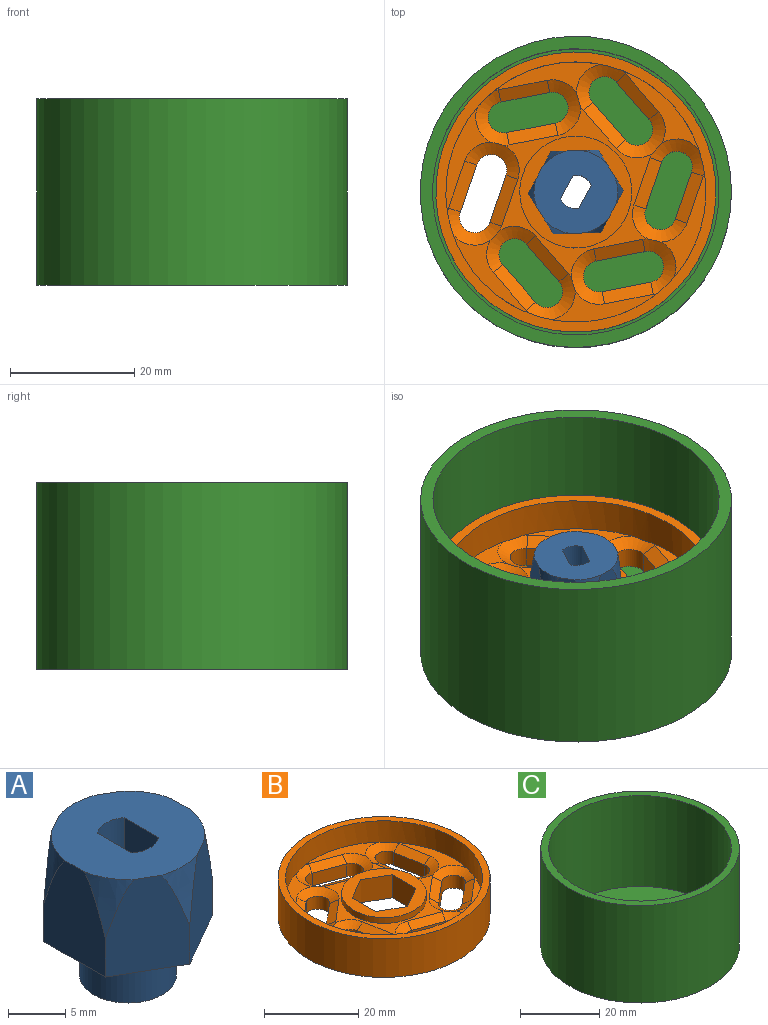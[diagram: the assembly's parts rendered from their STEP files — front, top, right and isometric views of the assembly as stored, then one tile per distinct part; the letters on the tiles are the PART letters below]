
ASSEMBLY  parts=3 mates=1
PART A: 21 faces, bbox 15.1x15.3x15 mm
  f0: plane 13.47x13.25mm, normal (0,0,1), area 124.8mm2, adj f1,f2,f3,f4,f5,f6,f7,f12
  f1: plane 10x6.63mm, normal (0.5,0.87,0), area 63.4mm2, adj f0,f2,f3,f14,f19,f20
  f2: plane 10x6.63mm, normal (-0.5,0.87,0), area 63.4mm2, adj f0,f1,f4,f14,f18,f20
  f3: plane 10x7.65mm, normal (1,0,0), area 63.4mm2, adj f0,f1,f5,f14,f17,f19
  f4: plane 10x7.65mm, normal (-1,0,0), area 63.4mm2, adj f0,f2,f6,f14,f15,f18
  f5: plane 10x6.63mm, normal (0.5,-0.87,0), area 63.4mm2, adj f0,f3,f6,f14,f16,f17
  f6: plane 10x6.63mm, normal (-0.5,-0.87,0), area 63.4mm2, adj f0,f4,f5,f14,f15,f16
  f7: cylinder r=2.7mm len=15mm, axis (0,0,-1), area 136.1mm2, adj f0,f9,f10,f11,f12,f13
  f8: cylinder r=4.25mm len=8.5mm, axis (0,0,-1), area 133.5mm2, adj f9,f14
  f9: plane 8.5x8.5mm, normal (0,0,-1), area 33.8mm2, adj f7,f8
  f10: plane 4.27x1.05mm, normal (0,0,-1), area 3.1mm2, adj f7,f13
  f11: plane 4.27x1.05mm, normal (0,0,-1), area 3.1mm2, adj f7,f12
  f12: plane 12x4.27mm, normal (-1,0,0), area 51.3mm2, adj f0,f7,f11
  f13: plane 12x4.27mm, normal (1,0,0), area 51.3mm2, adj f0,f7,f10
  f14: plane 15.3x13.25mm, normal (0,0,-1), area 95.3mm2, adj f1,f2,f3,f4,f5,f6,f8
  f15: cone r=6.59mm half-angle=8.8deg, axis (0,0,-1), area 11.5mm2, adj f0,f4,f6
  f16: cone r=6.59mm half-angle=8.8deg, axis (0,0,-1), area 11.5mm2, adj f0,f5,f6
  f17: cone r=6.59mm half-angle=8.8deg, axis (0,0,-1), area 11.5mm2, adj f0,f3,f5
  f18: cone r=6.59mm half-angle=8.8deg, axis (0,0,-1), area 11.5mm2, adj f0,f2,f4
  f19: cone r=6.59mm half-angle=8.8deg, axis (0,0,-1), area 11.5mm2, adj f0,f1,f3
  f20: cone r=6.59mm half-angle=8.8deg, axis (0,0,-1), area 11.5mm2, adj f0,f1,f2
PART B: 67 faces, bbox 45x45x10 mm
  f0: plane 17.26x5.04mm, normal (0,0,1), area 34mm2, adj f41,f62,f64,f65,f66
  f1: plane 17.26x5.04mm, normal (0,0,1), area 34mm2, adj f41,f43,f45,f46,f47
  f2: plane 12.95x12.08mm, normal (0,0,1), area 34mm2, adj f41,f54,f56,f59,f62
  f3: plane 16.94x7.36mm, normal (0,0,1), area 34mm2, adj f41,f46,f48,f51,f54
  f4: plane 12.95x12.08mm, normal (0,0,1), area 34mm2, adj f41,f47,f50,f53,f55
  f5: plane 16.94x7.36mm, normal (0,0,1), area 34mm2, adj f41,f55,f58,f61,f64
  f6: cylinder r=2.5mm len=4.96mm, axis (0,0,-1), area 26.3mm2, adj f7,f24,f32,f65
  f7: plane 7.88x3.35mm, normal (-0.98,-0.17,0), area 26.8mm2, adj f6,f8,f32,f63
  f8: cylinder r=2.5mm len=4.96mm, axis (0,0,-1), area 26.3mm2, adj f7,f24,f32,f64
  f9: cylinder r=2.5mm len=4.42mm, axis (0,0,-1), area 26.3mm2, adj f10,f25,f32,f56
  f10: plane 6.13x5.14mm, normal (-0.64,0.77,0), area 26.8mm2, adj f9,f11,f32,f60
  f11: cylinder r=2.5mm len=4.42mm, axis (0,0,-1), area 26.3mm2, adj f10,f25,f32,f62
  f12: cylinder r=2.5mm len=4.85mm, axis (0,0,-1), area 26.3mm2, adj f13,f26,f32,f48
  f13: plane 7.52x3.35mm, normal (0.34,0.94,0), area 26.8mm2, adj f12,f14,f32,f52
  f14: cylinder r=2.5mm len=4.85mm, axis (0,0,-1), area 26.3mm2, adj f13,f26,f32,f54
  f15: cylinder r=2.5mm len=4.96mm, axis (0,0,-1), area 26.3mm2, adj f16,f27,f32,f45
  f16: plane 7.88x3.35mm, normal (0.98,0.17,0), area 26.8mm2, adj f15,f17,f32,f44
  f17: cylinder r=2.5mm len=4.96mm, axis (0,0,-1), area 26.3mm2, adj f16,f27,f32,f46
  f18: cylinder r=2.5mm len=4.42mm, axis (0,0,-1), area 26.3mm2, adj f19,f28,f32,f53
  f19: plane 6.13x5.14mm, normal (0.64,-0.77,0), area 26.8mm2, adj f18,f20,f32,f49
  f20: cylinder r=2.5mm len=4.42mm, axis (0,0,-1), area 26.3mm2, adj f19,f28,f32,f47
  f21: cylinder r=2.5mm len=4.85mm, axis (0,0,-1), area 26.3mm2, adj f22,f29,f32,f61
  f22: plane 7.52x3.35mm, normal (-0.34,-0.94,0), area 26.8mm2, adj f21,f23,f32,f57
  f23: cylinder r=2.5mm len=4.85mm, axis (0,0,-1), area 26.3mm2, adj f22,f29,f32,f55
  f24: plane 7.88x3.35mm, normal (0.98,0.17,0), area 26.8mm2, adj f6,f8,f32,f66
  f25: plane 6.13x5.14mm, normal (0.64,-0.77,0), area 26.8mm2, adj f9,f11,f32,f59
  f26: plane 7.52x3.35mm, normal (-0.34,-0.94,0), area 26.8mm2, adj f12,f14,f32,f51
  f27: plane 7.88x3.35mm, normal (-0.98,-0.17,0), area 26.8mm2, adj f15,f17,f32,f43
  f28: plane 6.13x5.14mm, normal (-0.64,0.77,0), area 26.8mm2, adj f18,f20,f32,f50
  f29: plane 7.52x3.35mm, normal (0.34,0.94,0), area 26.8mm2, adj f21,f23,f32,f58
  f30: cylinder r=22.5mm len=45mm, axis (0,0,-1), area 1413.7mm2, adj f32,f42
  f31: plane 27.41x24.73mm, normal (0,0,1), area 106.8mm2, adj f33,f44,f45,f46,f47,f48,f49,f52
  f32: plane 45x45mm, normal (0,0,-1), area 1105.3mm2, adj f6,f7,f8,f9,f10,f11,f12,f13
  f33: cylinder r=9mm len=18mm, axis (0,0,-1), area 84.8mm2, adj f31,f34
  f34: plane 18x18mm, normal (0,0,1), area 127.2mm2, adj f33,f35,f36,f37,f38,f39,f40
  f35: plane 6.06x6mm, normal (0.5,0.87,0), area 42mm2, adj f32,f34,f36,f38
  f36: plane 7x6mm, normal (1,0,0), area 42mm2, adj f32,f34,f35,f37
  f37: plane 6.06x6mm, normal (0.5,-0.87,0), area 42mm2, adj f32,f34,f36,f39
  f38: plane 6.06x6mm, normal (-0.5,0.87,0), area 42mm2, adj f32,f34,f35,f40
  f39: plane 6.06x6mm, normal (-0.5,-0.87,0), area 42mm2, adj f32,f34,f37,f40
  f40: plane 7x6mm, normal (-1,0,0), area 42mm2, adj f32,f34,f38,f39
  f41: cylinder r=20.9mm len=41.8mm, axis (0,0,-1), area 724.7mm2, adj f0,f1,f2,f3,f4,f5,f42,f46
  f42: plane 45x45mm, normal (0,0,1), area 218.2mm2, adj f30,f41
  f43: plane 8.23x3.36mm, normal (-0.49,-0.09,0.87), area 18.5mm2, adj f1,f27,f45,f46
  f44: plane 8.23x3.36mm, normal (0.49,0.09,0.87), area 18.5mm2, adj f16,f31,f45,f46
  f45: cone r=2.5mm half-angle=60deg, axis (0,0,1), area 25.1mm2, adj f1,f15,f31,f43,f44,f47
  f46: cone r=2.5mm half-angle=60deg, axis (0,0,1), area 24.3mm2, adj f1,f3,f17,f31,f41,f43,f44,f48
  f47: cone r=2.5mm half-angle=60deg, axis (0,0,1), area 24.3mm2, adj f1,f4,f20,f31,f41,f45,f49,f50
  f48: cone r=2.5mm half-angle=60deg, axis (0,0,1), area 25.1mm2, adj f3,f12,f31,f46,f51,f52
  f49: plane 7.41x6.67mm, normal (0.32,-0.38,0.87), area 18.5mm2, adj f19,f31,f47,f53
  f50: plane 7.41x6.67mm, normal (-0.32,0.38,0.87), area 18.5mm2, adj f4,f28,f47,f53
  f51: plane 8.2x4.62mm, normal (-0.17,-0.47,0.87), area 18.5mm2, adj f3,f26,f48,f54
  f52: plane 8.2x4.62mm, normal (0.17,0.47,0.87), area 18.5mm2, adj f13,f31,f48,f54
  f53: cone r=2.5mm half-angle=60deg, axis (0,0,1), area 25.1mm2, adj f4,f18,f31,f49,f50,f55
  f54: cone r=2.5mm half-angle=60deg, axis (0,0,1), area 24.3mm2, adj f2,f3,f14,f31,f41,f51,f52,f56
  f55: cone r=2.5mm half-angle=60deg, axis (0,0,1), area 24.3mm2, adj f4,f5,f23,f31,f41,f53,f57,f58
  f56: cone r=2.5mm half-angle=60deg, axis (0,0,1), area 25.1mm2, adj f2,f9,f31,f54,f59,f60
  f57: plane 8.2x4.62mm, normal (-0.17,-0.47,0.87), area 18.5mm2, adj f22,f31,f55,f61
  f58: plane 8.2x4.62mm, normal (0.17,0.47,0.87), area 18.5mm2, adj f5,f29,f55,f61
  f59: plane 7.41x6.67mm, normal (0.32,-0.38,0.87), area 18.5mm2, adj f2,f25,f56,f62
  f60: plane 7.41x6.67mm, normal (-0.32,0.38,0.87), area 18.5mm2, adj f10,f31,f56,f62
  f61: cone r=2.5mm half-angle=60deg, axis (0,0,1), area 25.1mm2, adj f5,f21,f31,f57,f58,f64
  f62: cone r=2.5mm half-angle=60deg, axis (0,0,1), area 24.3mm2, adj f0,f2,f11,f31,f41,f59,f60,f65
  f63: plane 8.23x3.36mm, normal (-0.49,-0.09,0.87), area 18.5mm2, adj f7,f31,f64,f65
  f64: cone r=2.5mm half-angle=60deg, axis (0,0,1), area 24.3mm2, adj f0,f5,f8,f31,f41,f61,f63,f66
  f65: cone r=2.5mm half-angle=60deg, axis (0,0,1), area 25.1mm2, adj f0,f6,f31,f62,f63,f66
  f66: plane 8.23x3.36mm, normal (0.49,0.09,0.87), area 18.5mm2, adj f0,f24,f64,f65
PART C: 12 faces, bbox 50x50x30 mm
  f0: cylinder r=21mm len=21mm, axis (0,0,-1), area 44mm2, adj f1,f3,f4,f5
  f1: plane 9.53x5.5mm, normal (-0.5,-0.87,0), area 22mm2, adj f0,f2,f4,f5
  f2: cylinder r=10mm len=10mm, axis (0,0,-1), area 20.9mm2, adj f1,f3,f4,f5
  f3: plane 9.53x5.5mm, normal (-0.5,0.87,0), area 22mm2, adj f0,f2,f4,f5
  f4: plane 46x46mm, normal (0,0,1), area 1282.3mm2, adj f0,f1,f2,f3,f6,f9
  f5: plane 50x50mm, normal (0,0,-1), area 1631mm2, adj f0,f1,f2,f3,f7,f10
  f6: cylinder r=8mm len=16mm, axis (0,0,-1), area 150.8mm2, adj f4,f8
  f7: cylinder r=7mm len=14mm, axis (0,0,-1), area 219.9mm2, adj f5,f8
  f8: plane 16x16mm, normal (0,0,1), area 47.1mm2, adj f6,f7
  f9: cylinder r=23mm len=46mm, axis (0,0,-1), area 4046.4mm2, adj f4,f11
  f10: cylinder r=25mm len=50mm, axis (0,0,-1), area 4712.4mm2, adj f5,f11
  f11: plane 50x50mm, normal (0,0,1), area 301.6mm2, adj f9,f10
PLACE A rot(axis=(0,0,-1),28.2deg) t=(15.87,-26.68,9)mm
PLACE B rot(axis=(0,0,-1),149deg) t=(15.87,-26.68,8)mm
PLACE C t=(15.87,-26.68,5)mm fixed
MATE revolute C.f0 <-> B.f30  axis (0,0,-1) through (15.87,-26.68,10)mm
